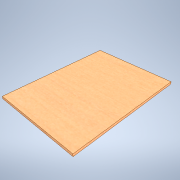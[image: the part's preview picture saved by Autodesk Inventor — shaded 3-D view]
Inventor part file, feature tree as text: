
AUTODESK INVENTOR PART (.ipt)
format: ipt  version: 2021 (Build 250183000, 183)  size: 104,960 bytes
history: native  units: mm
features: extrude x1, sketch x1
ambient origin geometry x8: Origin, YZ Plane, XZ Plane, XY Plane, X Axis, Y Axis, Z Axis, Center Point
bodies: Solid1 (feature_tree)
feature tree (2):
  extrude  "Extrusion1"  Depth=134.0mm
  sketch  "Sketch1"  dims[d0=99.0mm d1=134.0mm d2=3.0mm d3=0.0mm]
